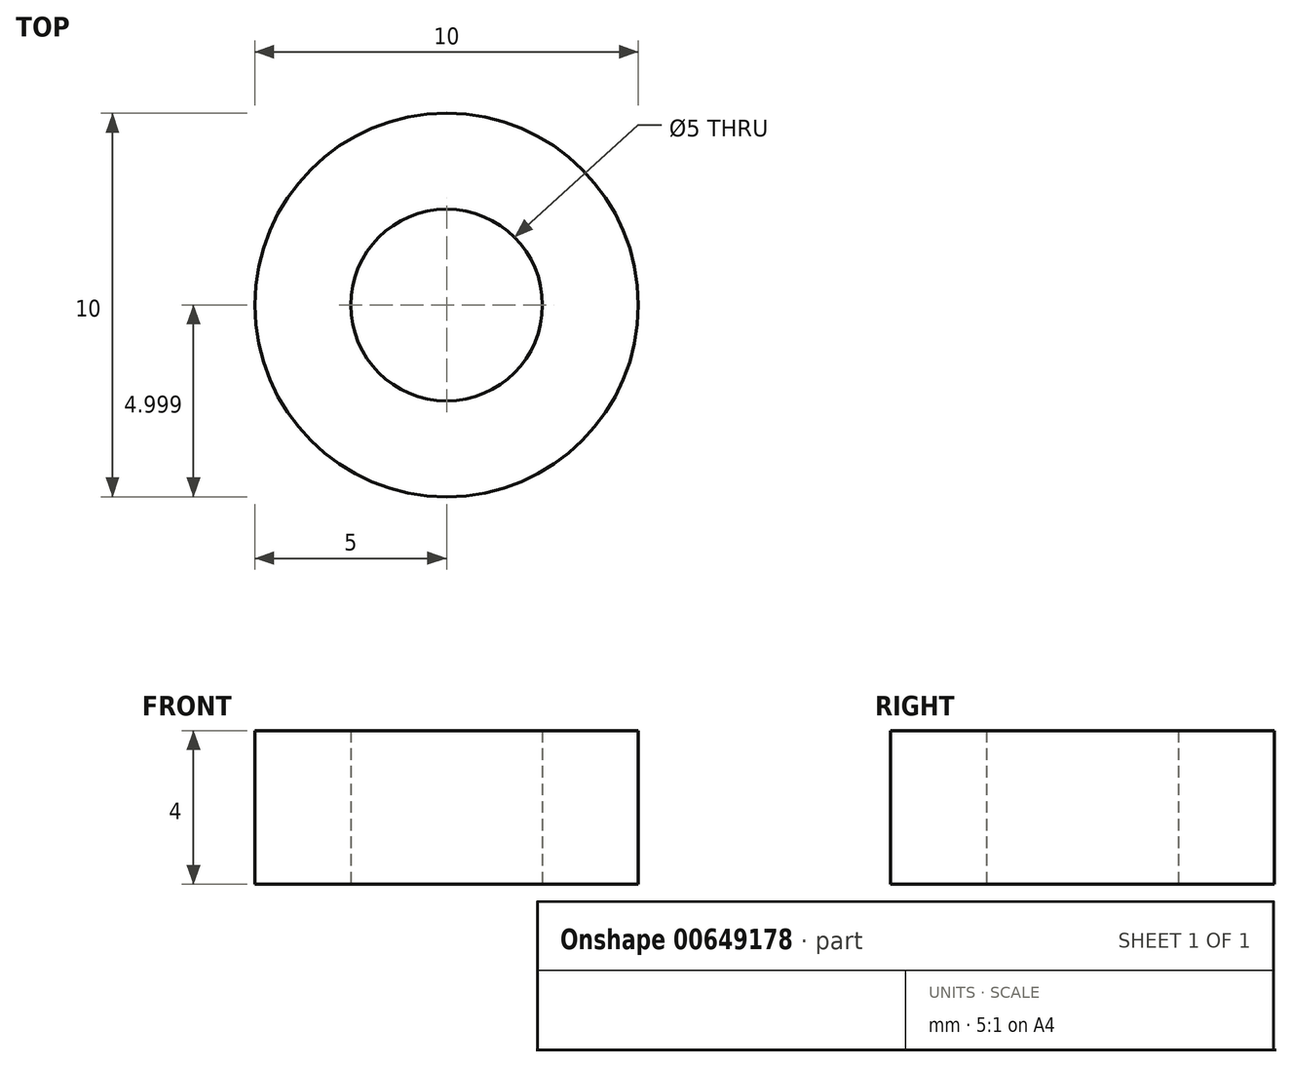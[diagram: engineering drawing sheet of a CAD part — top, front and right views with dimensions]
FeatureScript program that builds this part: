
annotation { "Feature Type Name" : "Feature", "Feature Type Description" : "" }
export const myFeature = defineFeature(function(context is Context, id is Id, definition is map)
    precondition{}
    {
        {
            var Q0;
            Q0=qCreatedBy(makeId("Top.planeOp"),FACE);
            var sketch = newSketch(context, id + "F0", { "sketchPlane" : qUnion([Q0])});
            skCircle(sketch, "E0", {"center": v(0, 0.17) * mm, "radius": 2.5 * mm});
            skCircle(sketch, "E1", {"center": v(0, 0.17) * mm, "radius": 5 * mm});
            skSolve(sketch);
        }
        {
            var Q0;
            Q0=qSketchRegion(id+"F0",true);
            extrude(context, id + "F1", {"entities" : qUnion([Q0]), "depth" : 4 * mm});
        }
    });
